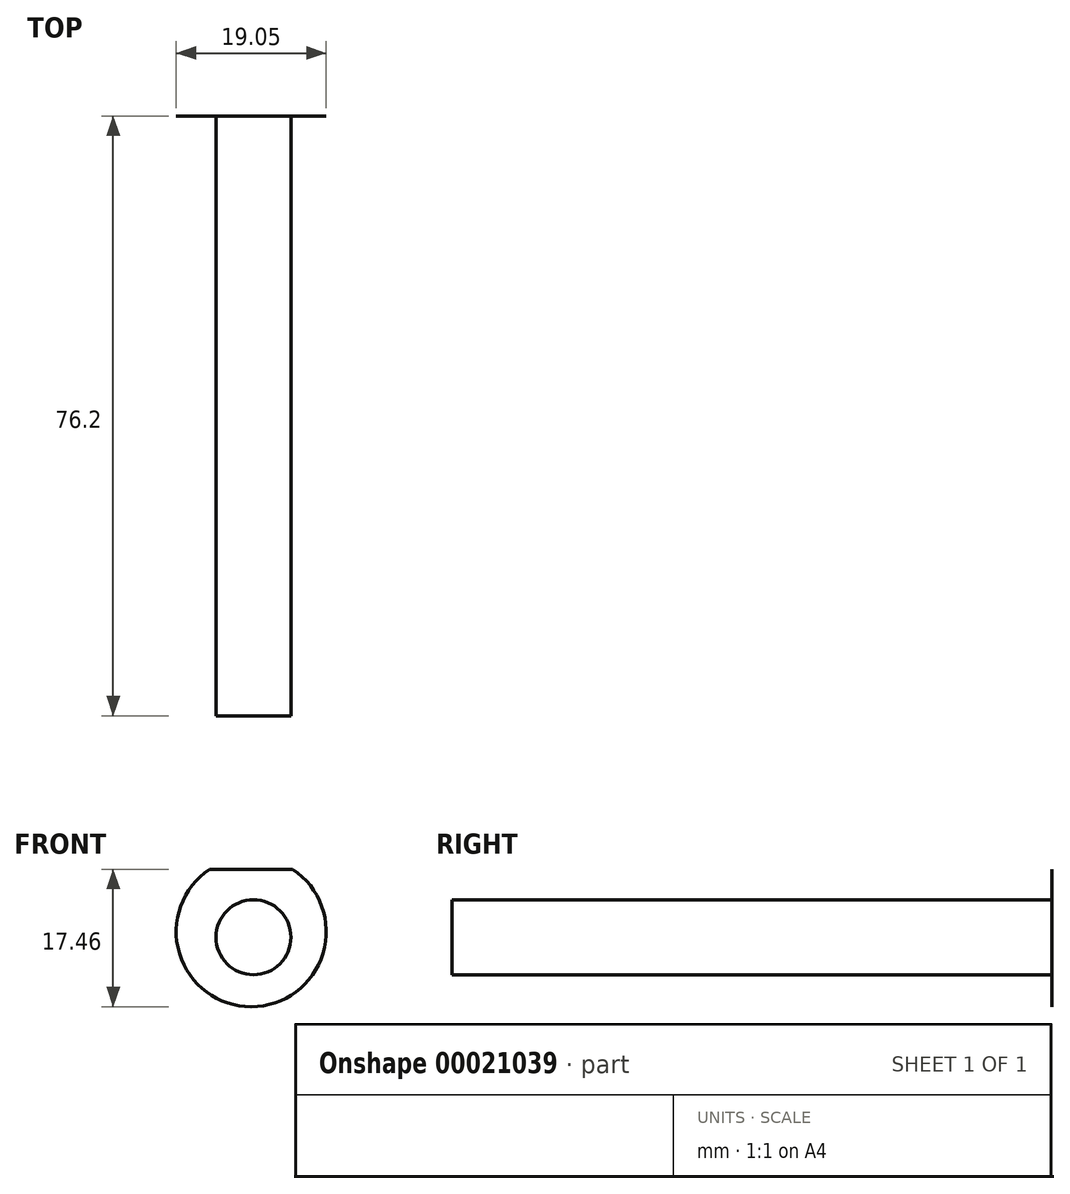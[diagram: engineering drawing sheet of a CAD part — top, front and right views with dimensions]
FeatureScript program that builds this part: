
annotation { "Feature Type Name" : "Feature", "Feature Type Description" : "" }
export const myFeature = defineFeature(function(context is Context, id is Id, definition is map)
    precondition{}
    {
        {
            var Q0;
            Q0=qCreatedBy(makeId("Front.planeOp"),FACE);
            var sketch = newSketch(context, id + "F0", { "sketchPlane" : qUnion([Q0])});
            skCircle(sketch, "E0", {"center": v(-105.16, 20.9) * mm, "radius": 4.76 * mm});
            skSolve(sketch);
        }
        {
            var Q0;
            Q0=makeQuery(id+"F0.imprint","IMPRINT",FACE,{"disambiguationData":[TD([[makeQuery(id+"F0.imprint","IMPRINT",EDGE,{"derivedFrom":sQuery(id+"F0.wireOp",EDGE,"E0")}),1.0]])]});
            extrude(context, id + "F1", {"entities" : qUnion([Q0]), "depth" : 76.2 * mm});
        }
        {
            var Q0;
            Q0=qCreatedBy(makeId("Front.planeOp"),FACE);
            var sketch = newSketch(context, id + "F2", { "sketchPlane" : qUnion([Q0])});
            skCircle(sketch, "E1", {"center": v(-105.45, 21.6) * mm, "radius": 9.53 * mm});
            skSolve(sketch);
        }
        {
            var Q0;
            Q0=makeQuery(id+"F2.imprint","IMPRINT",FACE,{"disambiguationData":[TD([[makeQuery(id+"F2.imprint","IMPRINT",EDGE,{"derivedFrom":sQuery(id+"F2.wireOp",EDGE,"E1")}),1.0]])]});
            var Q1;
            Q1=makeQuery(id+"F1.opExtrude","CAP_FACE",FACE,{"disambiguationData":[OSD([sQuery(id+"F0.wireOp",EDGE,"E0")])],"isStart":true});
            extrude(context, id + "F3", {"entities" : qUnion([Q0, Q1]), "operationType" : NewBodyOperationType.ADD, "depth" : 1 / 406.4 * mm});
        }
        {
            var Q0;
            Q0=makeQuery(id+"F3.boolean.opBoolean","MERGE",FACE,{"derivedFrom":[makeQuery(id+"F3.opExtrude","CAP_FACE",FACE,{"disambiguationData":[OSD([sQuery(id+"F0.wireOp",EDGE,"E0")])],"isStart":false}),makeQuery(id+"F3.opExtrude","CAP_FACE",FACE,{"disambiguationData":[OSD([sQuery(id+"F2.wireOp",EDGE,"E1")])],"isStart":false})]});
            var sketch = newSketch(context, id + "F4", { "sketchPlane" : qUnion([Q0])});
            skLineSegment(sketch, "E2", {"start": v(-110.71, 29.53) * mm, "end": v(-100.18, 29.53) * mm});
            skSolve(sketch);
        }
        {
            var Q0;
            {var subQ1=sQuery(id+"F4.wireOp",EDGE,"E2");Q0=makeQuery(id+"F4.imprint","IMPRINT",FACE,{"disambiguationData":[TD([[makeQuery(id+"F4.imprint","IMPRINT",EDGE,{"derivedFrom":subQ1}),1.0]])]});}
            extrude(context, id + "F5", {"entities" : qUnion([Q0]), "operationType" : NewBodyOperationType.REMOVE, "oppositeDirection" : true, "depth" : 25.4 * mm});
        }
    });
